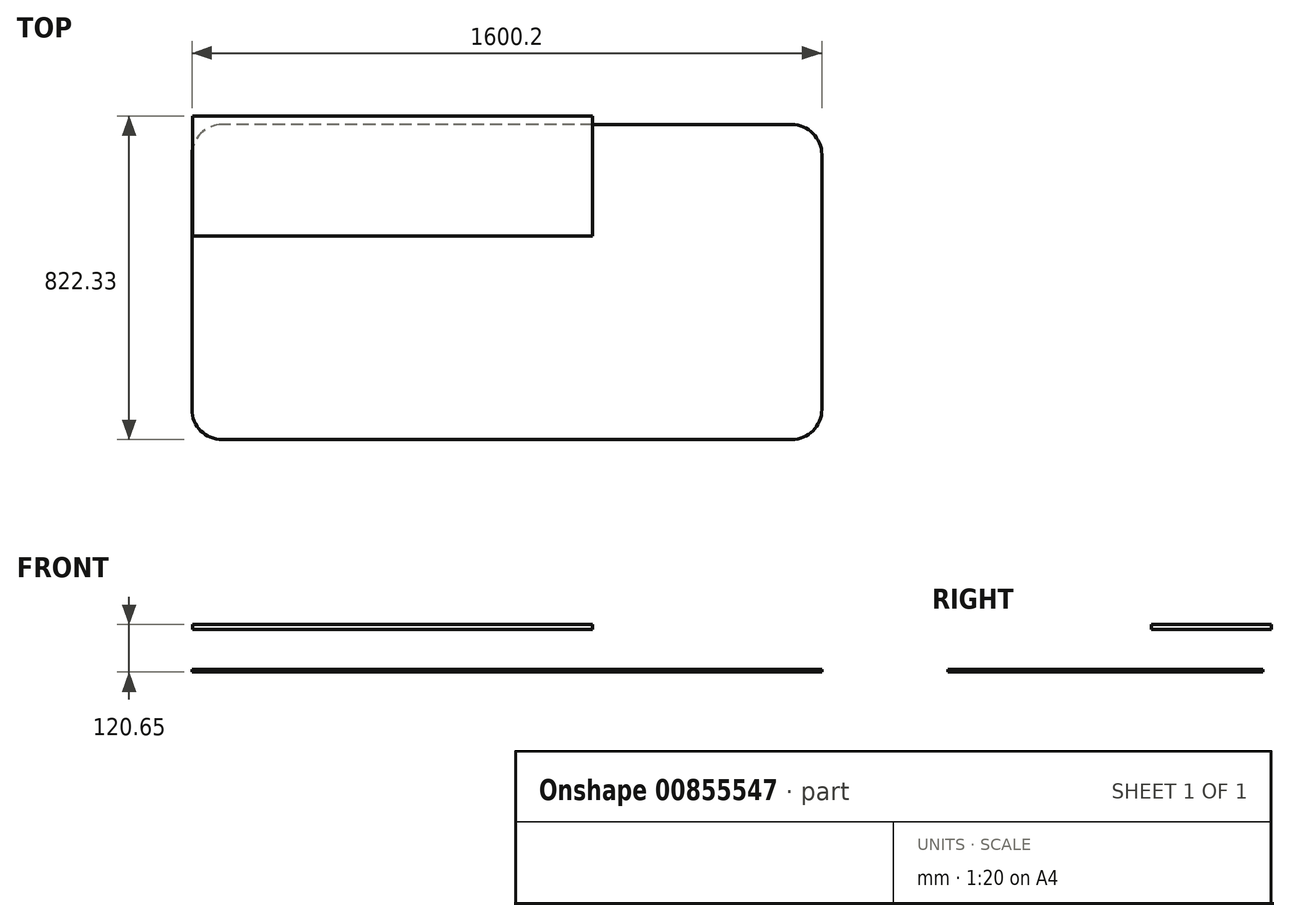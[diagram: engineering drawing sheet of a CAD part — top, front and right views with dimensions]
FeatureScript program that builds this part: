
annotation { "Feature Type Name" : "Feature", "Feature Type Description" : "" }
export const myFeature = defineFeature(function(context is Context, id is Id, definition is map)
    precondition{}
    {
        {
            var Q0;
            Q0=qCreatedBy(makeId("Top.planeOp"),FACE);
            var sketch = newSketch(context, id + "F0", { "sketchPlane" : qUnion([Q0])});
            skLineSegment(sketch, "E0.bottom", {"start": v(800.1, -400.05) * mm, "end": v(-800.1, -400.05) * mm});
            skLineSegment(sketch, "E0.top", {"start": v(800.1, 400.05) * mm, "end": v(-800.1, 400.05) * mm});
            skLineSegment(sketch, "E0.left", {"start": v(800.1, -400.05) * mm, "end": v(800.1, 400.05) * mm});
            skLineSegment(sketch, "E0.right", {"start": v(-800.1, -400.05) * mm, "end": v(-800.1, 400.05) * mm});
            skPoint(sketch, "E0.middle", {"position": v(0, 0) * mm});
            skSolve(sketch);
        }
        {
            var Q0;
            Q0=makeQuery(id+"F0.imprint","IMPRINT",FACE,{"disambiguationData":[TD([[makeQuery(id+"F0.imprint","IMPRINT",EDGE,{"derivedFrom":sQuery(id+"F0.wireOp",EDGE,"E0.bottom")}),-1.0]])]});
            extrude(context, id + "F1", {"entities" : qUnion([Q0]), "depth" : 6.35 * mm, "offsetDistance" : 25.4 * mm});
        }
        {
            var Q0;
            Q0=makeQuery(id+"F1.opExtrude","SWEPT_EDGE",EDGE,{"disambiguationData":[OSD([sQuery(id+"F0.wireOp",EDGE,"E0.bottom"),sQuery(id+"F0.wireOp",EDGE,"E0.right")])]});
            var Q1;
            Q1=makeQuery(id+"F1.opExtrude","SWEPT_EDGE",EDGE,{"disambiguationData":[OSD([sQuery(id+"F0.wireOp",EDGE,"E0.bottom"),sQuery(id+"F0.wireOp",EDGE,"E0.left")])]});
            var Q2;
            Q2=makeQuery(id+"F1.opExtrude","SWEPT_EDGE",EDGE,{"disambiguationData":[OSD([sQuery(id+"F0.wireOp",EDGE,"E0.top"),sQuery(id+"F0.wireOp",EDGE,"E0.right")])]});
            var Q3;
            Q3=makeQuery(id+"F1.opExtrude","SWEPT_EDGE",EDGE,{"disambiguationData":[OSD([sQuery(id+"F0.wireOp",EDGE,"E0.top"),sQuery(id+"F0.wireOp",EDGE,"E0.left")])]});
            fillet(context, id + "F2", {"entities" : qUnion([Q0, Q1, Q2, Q3]), "radius" : 76.2 * mm, "tangentPropagation" : true, "allowEdgeOverflow" : false});
        }
        {
            var Q0;
            Q0=makeQuery(id+"F1.opExtrude","CAP_FACE",FACE,{"disambiguationData":[OSD([sQuery(id+"F0.wireOp",EDGE,"E0.bottom"),sQuery(id+"F0.wireOp",EDGE,"E0.top"),sQuery(id+"F0.wireOp",EDGE,"E0.left"),sQuery(id+"F0.wireOp",EDGE,"E0.right")])],"isStart":false});
            cPlane(context, id + "F3", {"entities" : qUnion([Q0]), "cplaneType" : CPlaneType.OFFSET, "offset" : 101.6 * mm, "width" : 152.4 * mm, "height" : 152.4 * mm});
        }
        {
            var Q0;
            Q0=qCreatedBy(id+"F3.planeOp",FACE);
            var sketch = newSketch(context, id + "F4", { "sketchPlane" : qUnion([Q0])});
            skLineSegment(sketch, "E1.bottom", {"start": v(217.07, 117.48) * mm, "end": v(-798.93, 117.48) * mm});
            skLineSegment(sketch, "E1.top", {"start": v(217.07, 422.28) * mm, "end": v(-798.93, 422.28) * mm});
            skLineSegment(sketch, "E1.left", {"start": v(217.07, 117.48) * mm, "end": v(217.07, 422.28) * mm});
            skLineSegment(sketch, "E1.right", {"start": v(-798.93, 117.48) * mm, "end": v(-798.93, 422.28) * mm});
            skPoint(sketch, "E1.middle", {"position": v(-290.93, 269.88) * mm});
            skSolve(sketch);
        }
        {
            var Q0;
            Q0=makeQuery(id+"F4.imprint","IMPRINT",FACE,{"disambiguationData":[TD([[makeQuery(id+"F4.imprint","IMPRINT",EDGE,{"derivedFrom":sQuery(id+"F4.wireOp",EDGE,"E1.bottom")}),-1.0]])]});
            extrude(context, id + "F5", {"entities" : qUnion([Q0]), "depth" : 12.7 * mm, "offsetDistance" : 25.4 * mm});
        }
    });
